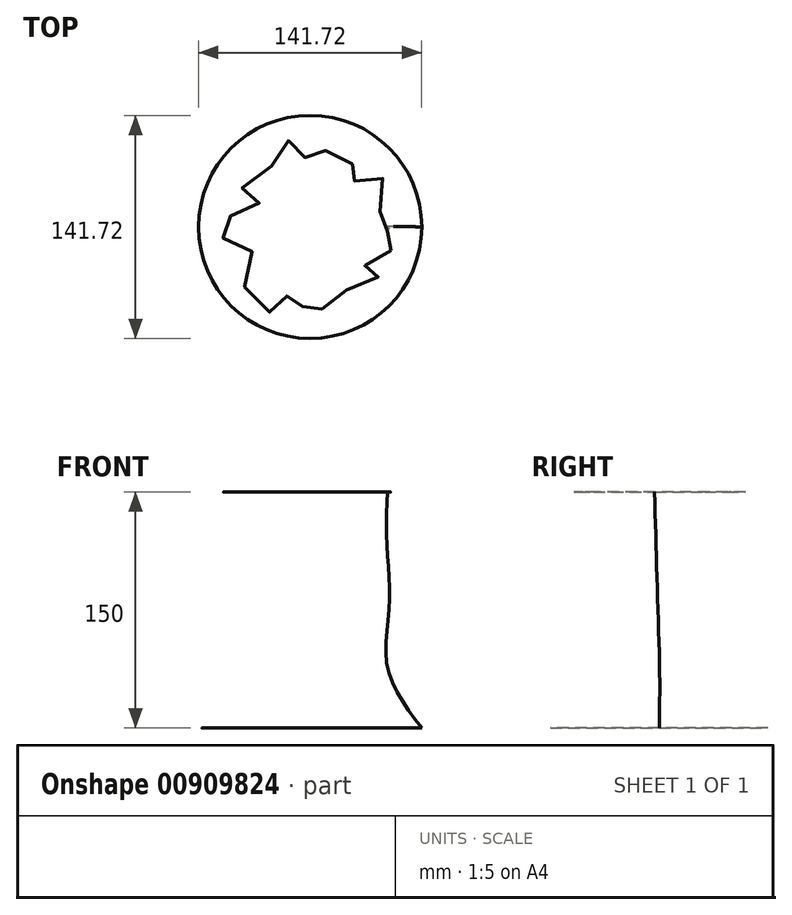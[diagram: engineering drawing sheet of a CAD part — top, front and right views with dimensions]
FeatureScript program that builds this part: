
annotation { "Feature Type Name" : "Feature", "Feature Type Description" : "" }
export const myFeature = defineFeature(function(context is Context, id is Id, definition is map)
    precondition{}
    {
        {
            var Q0;
            Q0=qCreatedBy(makeId("Top.planeOp"),FACE);
            var sketch = newSketch(context, id + "F0", { "sketchPlane" : qUnion([Q0])});
            skLineSegment(sketch, "E0", {"start": v(0, 60) * mm, "end": v(0, -60) * mm, "construction": true});
            skCircle(sketch, "E1", {"center": v(0, 0) * mm, "radius": 70.86 * mm});
            skSolve(sketch);
        }
        {
            var Q0;
            Q0=qCreatedBy(makeId("Top.planeOp"),FACE);
            cPlane(context, id + "F1", {"entities" : qUnion([Q0]), "cplaneType" : CPlaneType.OFFSET, "offset" : 40 * mm, "width" : 150 * mm, "height" : 150 * mm});
        }
        {
            var Q0;
            Q0=qCreatedBy(id+"F1.planeOp",FACE);
            var sketch = newSketch(context, id + "F2", { "sketchPlane" : qUnion([Q0])});
            skFitSpline(sketch, "E2", {"points": [v(-6.31, 54.6) * mm, v(-6.8, 41.4) * mm, v(-28.26, 38.48) * mm, v(-33.15, 29.75) * mm, v(-21.93, 28.44) * mm, v(-33.16, 16.76) * mm, v(-43.7, 18.82) * mm, v(-41.75, 8.7) * mm, v(-45.18, 5.23) * mm, v(-31.87, -6.96) * mm, v(-43, -22.3) * mm, v(-33.07, -27.46) * mm, v(-31.15, -36.2) * mm, v(-25.84, -34.17) * mm, v(-15.92, -34.46) * mm, v(-13.7, -42.8) * mm, v(-5.49, -38.16) * mm, v(-1.37, -44.68) * mm, v(7.27, -32.42) * mm, v(20.04, -36.54) * mm, v(28.06, -34.73) * mm, v(25.1, -27.7) * mm, v(34.6, -19.1) * mm, v(42.42, -19.02) * mm, v(43.53, -14.04) * mm, v(44.26, -6.46) * mm, v(48.72, 0.73) * mm, v(40.73, 3.95) * mm, v(46.7, 17) * mm, v(40.9, 25.73) * mm, v(29.1, 21.1) * mm, v(22.74, 31.32) * mm, v(26.24, 41.03) * mm, v(21.36, 47.71) * mm, v(10.84, 39.37) * mm, v(3.62, 48.17) * mm, v(1.6, 51.4) * mm, v(-6.31, 54.6) * mm]});
            skSolve(sketch);
        }
        {
            var Q0;
            Q0=qCreatedBy(id+"F1.planeOp",FACE);
            cPlane(context, id + "F3", {"entities" : qUnion([Q0]), "cplaneType" : CPlaneType.OFFSET, "offset" : 40 * mm, "width" : 150 * mm, "height" : 150 * mm});
        }
        {
            var Q0;
            Q0=qCreatedBy(id+"F3.planeOp",FACE);
            var sketch = newSketch(context, id + "F4", { "sketchPlane" : qUnion([Q0])});
            skFitSpline(sketch, "E3", {"points": [v(-34.16, 37.6) * mm, v(-33.89, 27.29) * mm, v(-45.02, 23.7) * mm, v(-41.53, 16.37) * mm, v(-40.94, 10.3) * mm, v(-44.56, -0.22) * mm, v(-49.34, -3.73) * mm, v(-46.36, -11.17) * mm, v(-45.76, -21.3) * mm, v(-32, -23.84) * mm, v(-37.93, -32.7) * mm, v(-21.26, -41.18) * mm, v(-16.04, -46.15) * mm, v(-11.98, -42.77) * mm, v(-1.52, -37.67) * mm, v(1.05, -42.6) * mm, v(6.8, -37.52) * mm, v(16.3, -39.51) * mm, v(19.42, -25.6) * mm, v(33.23, -24.06) * mm, v(43.21, -18.7) * mm, v(31.2, -11.1) * mm, v(40.86, -4.57) * mm, v(50.85, -0.03) * mm, v(48.63, 10.59) * mm, v(44.98, 14.7) * mm, v(42.85, 24.4) * mm, v(32.04, 28.35) * mm, v(34.18, 39.72) * mm, v(24.13, 41.6) * mm, v(13.17, 36.46) * mm, v(8.72, 44.1) * mm, v(4.24, 47.47) * mm, v(0.16, 52.81) * mm, v(-8.56, 45.98) * mm, v(-17.2, 41.22) * mm, v(-27.94, 46.94) * mm, v(-34.16, 37.6) * mm]});
            skSolve(sketch);
        }
        {
            var Q0;
            Q0=qCreatedBy(id+"F3.planeOp",FACE);
            cPlane(context, id + "F5", {"entities" : qUnion([Q0]), "cplaneType" : CPlaneType.OFFSET, "offset" : 40 * mm, "width" : 150 * mm, "height" : 150 * mm});
        }
        {
            var Q0;
            Q0=qCreatedBy(id+"F5.planeOp",FACE);
            var sketch = newSketch(context, id + "F6", { "sketchPlane" : qUnion([Q0])});
            skFitSpline(sketch, "E4", {"points": [v(-6.46, 51.67) * mm, v(-6.96, 38.48) * mm, v(-28.4, 35.55) * mm, v(-33.3, 26.83) * mm, v(-22.08, 25.51) * mm, v(-33.3, 13.83) * mm, v(-43.85, 15.9) * mm, v(-41.9, 5.77) * mm, v(-45.33, 2.3) * mm, v(-32.02, -9.9) * mm, v(-43.14, -25.23) * mm, v(-33.22, -30.39) * mm, v(-31.3, -39.13) * mm, v(-25.98, -37.1) * mm, v(-16.06, -37.39) * mm, v(-13.85, -45.74) * mm, v(-5.64, -41.1) * mm, v(-1.51, -47.61) * mm, v(7.12, -35.35) * mm, v(19.9, -39.46) * mm, v(27.91, -37.66) * mm, v(24.95, -30.63) * mm, v(34.45, -22.03) * mm, v(42.28, -21.95) * mm, v(43.38, -16.97) * mm, v(44.12, -9.4) * mm, v(48.57, -2.2) * mm, v(40.59, 1.02) * mm, v(46.56, 14.06) * mm, v(40.75, 22.8) * mm, v(28.95, 18.17) * mm, v(22.6, 28.39) * mm, v(26.1, 38.1) * mm, v(21.21, 44.79) * mm, v(10.7, 36.44) * mm, v(3.47, 45.24) * mm, v(1.46, 48.48) * mm, v(-6.46, 51.67) * mm]});
            skSolve(sketch);
        }
        {
            var Q0;
            Q0=qCreatedBy(id+"F5.planeOp",FACE);
            cPlane(context, id + "F7", {"entities" : qUnion([Q0]), "cplaneType" : CPlaneType.OFFSET, "offset" : 30 * mm, "width" : 150 * mm, "height" : 150 * mm});
        }
        {
            var Q0;
            Q0=qCreatedBy(id+"F7.planeOp",FACE);
            var sketch = newSketch(context, id + "F8", { "sketchPlane" : qUnion([Q0])});
            skLineSegment(sketch, "E5", {"start": v(1.92, 53.6) * mm, "end": v(1.92, -66.4) * mm, "construction": true});
            skFitSpline(sketch, "E6", {"points": [v(-19.62, 51.44) * mm, v(-23.59, 39.53) * mm, v(-40.88, 29.89) * mm, v(-41.03, 18.97) * mm, v(-32.52, 16.56) * mm, v(-39.6, 7.91) * mm, v(-52.8, 6.5) * mm, v(-55.91, -0.45) * mm, v(-52.5, -10.37) * mm, v(-37.06, -15.05) * mm, v(-42.3, -30.65) * mm, v(-34.93, -47.8) * mm, v(-24.3, -53.75) * mm, v(-18.91, -44.96) * mm, v(-13.52, -44.82) * mm, v(-8.42, -53.19) * mm, v(-3.32, -50.07) * mm, v(5.19, -56.73) * mm, v(11.29, -40.71) * mm, v(30.7, -40.43) * mm, v(43.47, -32.06) * mm, v(31.7, -29.94) * mm, v(37.37, -22.85) * mm, v(49.14, -18.45) * mm, v(50.84, -10.37) * mm, v(46.16, -6.26) * mm, v(54.38, 2.67) * mm, v(44.17, 10.04) * mm, v(47.72, 23.8) * mm, v(39.35, 35.56) * mm, v(26.6, 28.75) * mm, v(21.2, 33.3) * mm, v(27.73, 42.36) * mm, v(11, 49.03) * mm, v(3.91, 40.95) * mm, v(-4.03, 45.48) * mm, v(-6.15, 54.27) * mm, v(-19.62, 51.44) * mm]});
            skSolve(sketch);
        }
        {
            var Q0;
            Q0=makeQuery(id+"F0.imprint","IMPRINT",FACE,{"disambiguationData":[TD([[makeQuery(id+"F0.imprint","IMPRINT",EDGE,{"derivedFrom":sQuery(id+"F0.wireOp",EDGE,"E1")}),1.0]])]});
            var Q1;
            Q1=makeQuery(id+"F2.imprint","IMPRINT",FACE,{"disambiguationData":[TD([[makeQuery(id+"F2.imprint","IMPRINT",EDGE,{"derivedFrom":sQuery(id+"F2.wireOp",EDGE,"E2")}),1.0]])]});
            var Q2;
            Q2=makeQuery(id+"F4.imprint","IMPRINT",FACE,{"disambiguationData":[TD([[makeQuery(id+"F4.imprint","IMPRINT",EDGE,{"derivedFrom":sQuery(id+"F4.wireOp",EDGE,"E3")}),1.0]])]});
            var Q3;
            Q3=makeQuery(id+"F6.imprint","IMPRINT",FACE,{"disambiguationData":[TD([[makeQuery(id+"F6.imprint","IMPRINT",EDGE,{"derivedFrom":sQuery(id+"F6.wireOp",EDGE,"E4")}),1.0]])]});
            var Q4;
            Q4=makeQuery(id+"F8.imprint","IMPRINT",FACE,{"disambiguationData":[TD([[makeQuery(id+"F8.imprint","IMPRINT",EDGE,{"derivedFrom":sQuery(id+"F8.wireOp",EDGE,"E6")}),1.0]])]});
            loft(context, id + "F9", {"bodyType" : ToolBodyType.SURFACE, "wireProfilesArray" : [{ "wireProfileEntities" : qUnion([Q0]) }, { "wireProfileEntities" : qUnion([Q1]) }, { "wireProfileEntities" : qUnion([Q2]) }, { "wireProfileEntities" : qUnion([Q3]) }, { "wireProfileEntities" : qUnion([Q4]) }]});
        }
    });
